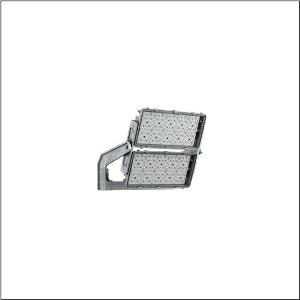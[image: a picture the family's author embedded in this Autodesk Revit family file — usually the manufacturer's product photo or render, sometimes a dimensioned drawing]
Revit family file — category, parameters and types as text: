
# Revit family: floodlight_fl_11_maxi_remote___rs07_5xa779514k01aa_47cf
name_source: partatom
category: Lighting Fixtures
units: mm (PartAtom-declared; Revit-internal decimal feet)

## family parameters
Cut with Voids When Loaded = No
Host = Face
Light Source = No
Part Type = Normal
Room Calculation Point = No
Round Connector Dimension = Use Diameter
Shared = No

## types (1)
- --- (1 x LED, 88570 lm, 916.8 W, 5700K)
    Apparent Load = 917 VA
    CIE Flux Codes = 80 93 99 100 99
    Color Rendering = 90
    Color Temperature = 5700K
    Default Elevation = 1800 mm
    Description = Floodlight FL 11  maxi  Remote floodlight; light control with lens of PMMA; cover panel of toughened safety glass, transparent; light distribution: RS07, rotationally symmetric direct distribution, LEDcolour temperature: 5700K, rated luminous flux: 88.570lm, colour rendering: CRI > 90, light colour: 957; luminous efficacy: 97lm/W; brightness control: DMX+RDM; with terminal, 6-pole, max. 2.5mm², mains connection: 220..240V/380..400V AC, 50/60Hz, surge voltage resistance: line to ground: 10kV, ECG replaceable separately, no afterglow with DALI off / DMX off command, LED unit replaceable without ESD environment, dustproof LED module, dimming range 10..100%; 917W floodlight with 2x LED unit of diecast aluminium, coated grey; length: 713mm / width: 651mm / height: 338mm; mounting bracket, of diecast aluminium, uncoated, natural, equipment: Power, protection rating (complete): IP66; insulation class (complete): insulation class I (protective earthing); certification: CE, ENEC, VDE; ball protection: ball impact resistance with accessories, impact resistance: IK07; rated ambient temperature 10°C, only for outdoor installations, permissible operating ambient temperature: -40..+30°C, permissible storage temperature: -40..+85°C; packaging unit: 1 piece

Light Distribution: RS07
    Height = 320 mm
    Lamp = 1 x LED
    Lamp Light Flux = 88570 lm
    Lamp Power = 916.8 W
    Lamp count = 1
    Length = 712 mm
    Luminous efficacy = 97 lm/W
    Manufacturer = Siteco
    ModVariant = No
    Model = 5XA779514K01AA
    Mounting Place = Ceiling
    Mounting Type = Surface mounted
    Number of Poles = 1
    OnlyDefault = Yes
    Power Factor = 1
    Product Name = Floodlight FL 11 maxi Remote | RS07
    Product group = floodlight | ceiling mounted
    ProductGroupID = 302
    Protection Class = Protection class I
    Protection Degree = IP 66
    RLX_Detail_Level = 1
    RLX_Emergency_Light_Flux = 0 lm
    RLX_Emergency_Type = 0
    RLX_Emergency_Type_DB = No
    RlxData = <blob elided: 41173 chars, md5=08c6ee07>
    Socket = socket
    Standby Power = 0 W
    System Light Flux = 88570 lm
    System Power = 917 W
    Type Comments = factory setting: luminous flux: 100 % | dim-lin: 254 | 950 mA
    Type Image = l_1006788.jpg
    URL = http://relux.com
    VarID = @adj_152995
    Voltage = 0 V
    Weight = 0.00 kg
    Width = 655 mm

## geometry (parser evidence)
native form markers: Blend x4, Sweep x12
no freeform markers — native parametric forms only
